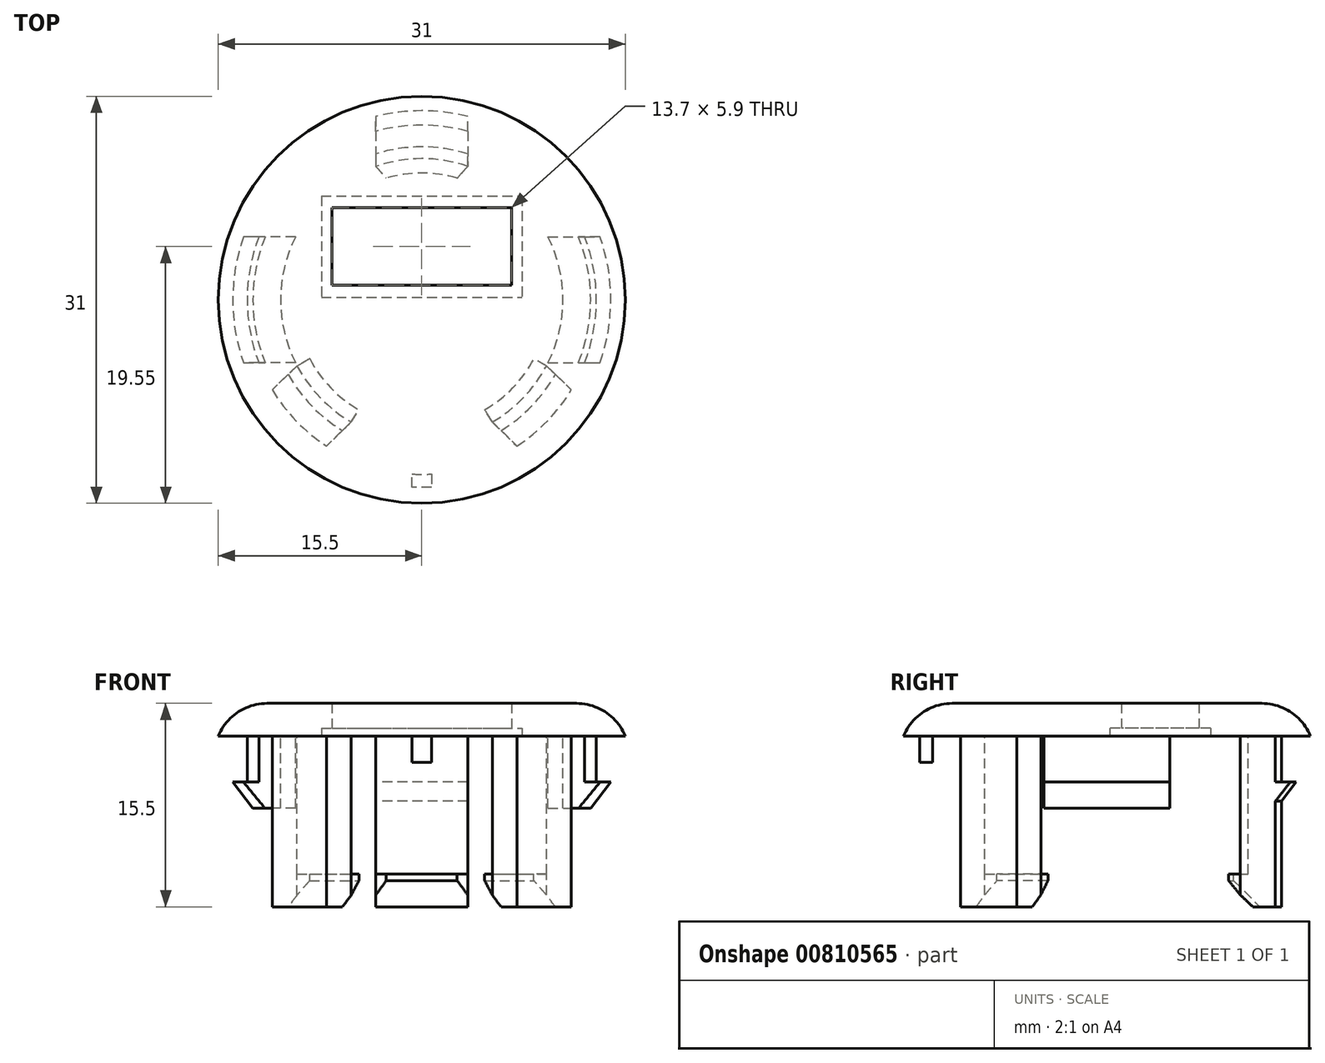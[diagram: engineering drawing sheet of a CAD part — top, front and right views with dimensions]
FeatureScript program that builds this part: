
annotation { "Feature Type Name" : "Feature", "Feature Type Description" : "" }
export const myFeature = defineFeature(function(context is Context, id is Id, definition is map)
    precondition{}
    {
        {
            var Q0;
            Q0=qCreatedBy(makeId("Top.planeOp"),FACE);
            var sketch = newSketch(context, id + "F0", { "sketchPlane" : qUnion([Q0])});
            skCircle(sketch, "E0", {"center": v(0, 0) * mm, "radius": 10.75 * mm});
            skLineSegment(sketch, "E1.bottom", {"start": v(-6.85, 7) * mm, "end": v(6.85, 7) * mm});
            skLineSegment(sketch, "E1.top", {"start": v(-6.85, 1.1) * mm, "end": v(6.85, 1.1) * mm});
            skLineSegment(sketch, "E1.left", {"start": v(-6.85, 7) * mm, "end": v(-6.85, 1.1) * mm});
            skLineSegment(sketch, "E1.right", {"start": v(6.85, 7) * mm, "end": v(6.85, 1.1) * mm});
            skPoint(sketch, "E1.middle", {"position": v(0, 4.05) * mm});
            skCircle(sketch, "E2", {"center": v(0, 0) * mm, "radius": 13.3 * mm});
            skLineSegment(sketch, "E3", {"start": v(-3.5, 12.83) * mm, "end": v(-3.5, 10.16) * mm});
            skLineSegment(sketch, "E4", {"start": v(3.5, 12.83) * mm, "end": v(3.5, 10.16) * mm});
            skLineSegment(sketch, "E5", {"start": v(9.5, -5.04) * mm, "end": v(11.4, -6.86) * mm});
            skLineSegment(sketch, "E6", {"start": v(5.37, -9.31) * mm, "end": v(7.25, -11.15) * mm});
            skLineSegment(sketch, "E7", {"start": v(-5.37, -9.31) * mm, "end": v(-7.25, -11.15) * mm});
            skLineSegment(sketch, "E8", {"start": v(-9.5, -5.04) * mm, "end": v(-11.4, -6.86) * mm});
            skPoint(sketch, "E9", {"position": v(-7.73, -7.47) * mm});
            skPoint(sketch, "E10", {"position": v(7.73, -7.47) * mm});
            skLineSegment(sketch, "E11", {"start": v(0, 0) * mm, "end": v(7.73, -7.47) * mm});
            skLineSegment(sketch, "E12", {"start": v(0, 0) * mm, "end": v(-7.73, -7.47) * mm});
            skLineSegment(sketch, "E13", {"start": v(-7.73, -7.47) * mm, "end": v(-9.57, -9.24) * mm});
            skLineSegment(sketch, "E14", {"start": v(7.73, -7.47) * mm, "end": v(9.57, -9.24) * mm});
            skCircle(sketch, "E15", {"center": v(0, 0) * mm, "radius": 9.65 * mm});
            skLineSegment(sketch, "E16", {"start": v(9.5, -5.04) * mm, "end": v(8.54, -4.5) * mm});
            skLineSegment(sketch, "E17", {"start": v(5.37, -9.31) * mm, "end": v(4.79, -8.38) * mm});
            skLineSegment(sketch, "E18", {"start": v(-5.37, -9.31) * mm, "end": v(-4.79, -8.38) * mm});
            skLineSegment(sketch, "E19", {"start": v(-9.5, -5.04) * mm, "end": v(-8.54, -4.5) * mm});
            skLineSegment(sketch, "E20", {"start": v(3.5, 10.16) * mm, "end": v(2.7, 9.26) * mm});
            skLineSegment(sketch, "E21", {"start": v(-3.5, 10.16) * mm, "end": v(-2.7, 9.26) * mm});
            skCircle(sketch, "E22", {"center": v(0, 0) * mm, "radius": 14.4 * mm});
            skLineSegment(sketch, "E23", {"start": v(9.62, -4.8) * mm, "end": v(12.4, -4.8) * mm});
            skLineSegment(sketch, "E24", {"start": v(12.4, -4.8) * mm, "end": v(13.58, -4.8) * mm});
            skLineSegment(sketch, "E25", {"start": v(9.62, 4.8) * mm, "end": v(12.4, 4.8) * mm});
            skLineSegment(sketch, "E26", {"start": v(12.4, 4.8) * mm, "end": v(13.58, 4.8) * mm});
            skLineSegment(sketch, "E27", {"start": v(-9.62, 4.8) * mm, "end": v(-12.4, 4.8) * mm});
            skLineSegment(sketch, "E28", {"start": v(-12.4, 4.8) * mm, "end": v(-13.58, 4.8) * mm});
            skLineSegment(sketch, "E29", {"start": v(-9.62, -4.8) * mm, "end": v(-12.4, -4.8) * mm});
            skLineSegment(sketch, "E30", {"start": v(-12.4, -4.8) * mm, "end": v(-13.58, -4.8) * mm});
            skLineSegment(sketch, "E31", {"start": v(0.75, -13.28) * mm, "end": v(0.75, -14.28) * mm});
            skLineSegment(sketch, "E32", {"start": v(0.75, -14.28) * mm, "end": v(-0.75, -14.28) * mm});
            skLineSegment(sketch, "E33", {"start": v(-0.75, -14.28) * mm, "end": v(-0.75, -13.28) * mm});
            skLineSegment(sketch, "E34.bottom", {"start": v(-7.65, 7.9) * mm, "end": v(7.65, 7.9) * mm});
            skLineSegment(sketch, "E34.top", {"start": v(-7.65, 0.2) * mm, "end": v(7.65, 0.2) * mm});
            skLineSegment(sketch, "E34.left", {"start": v(-7.65, 7.9) * mm, "end": v(-7.65, 0.2) * mm});
            skLineSegment(sketch, "E34.right", {"start": v(7.65, 7.9) * mm, "end": v(7.65, 0.2) * mm});
            skCircle(sketch, "E35", {"center": v(0, 0) * mm, "radius": 15.5 * mm});
            skLineSegment(sketch, "E36", {"start": v(-3.5, 12.83) * mm, "end": v(-3.5, 13.97) * mm});
            skLineSegment(sketch, "E37", {"start": v(3.5, 12.83) * mm, "end": v(3.5, 13.97) * mm});
            skSolve(sketch);
        }
        {
            var Q0;
            Q0=makeQuery(id+"F0.imprint","IMPRINT",FACE,{"disambiguationData":[TD([[makeQuery(id+"F0.imprint","IMPRINT",EDGE,{"derivedFrom":sQuery(id+"F0.wireOp",EDGE,"E0")}),1.0]])]});
            var Q1;
            Q1=makeQuery(id+"F0.imprint","IMPRINT",FACE,{"disambiguationData":[TD([[makeQuery(id+"F0.imprint","IMPRINT",EDGE,{"derivedFrom":sQuery(id+"F0.wireOp",EDGE,"E0")}),-1.0]])]});
            var Q2;
            {var subQ0=sQuery(id+"F0.wireOp",EDGE,"E11");Q2=makeQuery(id+"F0.imprint","IMPRINT",FACE,{"disambiguationData":[TD([[makeQuery(id+"F0.imprint","IMPRINT",EDGE,{"derivedFrom":subQ0}),-1.0]])]});}
            var Q3;
            Q3=makeQuery(id+"F0.imprint","IMPRINT",FACE,{"disambiguationData":[TD([[makeQuery(id+"F0.imprint","IMPRINT",EDGE,{"derivedFrom":sQuery(id+"F0.wireOp",EDGE,"E1.bottom")}),1.0]])]});
            var Q4;
            {var subQ2=sQuery(id+"F0.wireOp",EDGE,"E12");var subQ4=sQuery(id+"F0.wireOp",EDGE,"E11");var subQ5=makeQuery(id+"F0.imprint","INTERSECT",VERTEX,{"derivedFrom":[subQ4,subQ2]});Q4=makeQuery(id+"F0.imprint","IMPRINT",FACE,{"disambiguationData":[TD([[makeQuery(id+"F0.imprint","IMPRINT",EDGE,{"disambiguationData":[TD([[subQ5,-1.0]])],"derivedFrom":subQ4}),-1.0]])]});}
            var Q5;
            {var subQ9=sQuery(id+"F0.wireOp",EDGE,"E1.top");Q5=makeQuery(id+"F0.imprint","IMPRINT",FACE,{"disambiguationData":[TD([[makeQuery(id+"F0.imprint","IMPRINT",EDGE,{"derivedFrom":subQ9}),-1.0]])]});}
            var Q6;
            {var subQ5=sQuery(id+"F0.wireOp",EDGE,"E16");Q6=makeQuery(id+"F0.imprint","IMPRINT",FACE,{"disambiguationData":[TD([[makeQuery(id+"F0.imprint","IMPRINT",EDGE,{"derivedFrom":subQ5}),-1.0]])]});}
            var Q7;
            {var subQ8=sQuery(id+"F0.wireOp",EDGE,"E19");Q7=makeQuery(id+"F0.imprint","IMPRINT",FACE,{"disambiguationData":[TD([[makeQuery(id+"F0.imprint","IMPRINT",EDGE,{"derivedFrom":subQ8}),1.0]])]});}
            var Q8;
            Q8=makeQuery(id+"F0.imprint","IMPRINT",FACE,{"disambiguationData":[TD([[makeQuery(id+"F0.imprint","IMPRINT",EDGE,{"derivedFrom":sQuery(id+"F0.wireOp",EDGE,"E22")}),1.0]])]});
            var Q9;
            {var subQ0=sQuery(id+"F0.wireOp",EDGE,"E6");Q9=makeQuery(id+"F0.imprint","IMPRINT",FACE,{"disambiguationData":[TD([[makeQuery(id+"F0.imprint","IMPRINT",EDGE,{"derivedFrom":subQ0}),-1.0]])]});}
            var Q10;
            {var subQ4=sQuery(id+"F0.wireOp",EDGE,"V6FVYBft-MwFG-yFSS-5wyN-DWkYvqWRzlp1");Q10=makeQuery(id+"F0.imprint","IMPRINT",FACE,{"disambiguationData":[TD([[makeQuery(id+"F0.imprint","IMPRINT",EDGE,{"derivedFrom":subQ4}),1.0]])]});}
            var Q11;
            {var subQ0=sQuery(id+"F0.wireOp",EDGE,"V6FVYBft-MwFG-yFSS-5wyN-DWkYvqWRzlp1");Q11=makeQuery(id+"F0.imprint","IMPRINT",FACE,{"disambiguationData":[TD([[makeQuery(id+"F0.imprint","IMPRINT",EDGE,{"derivedFrom":subQ0}),-1.0]])]});}
            var Q12;
            {var subQ2=sQuery(id+"F0.wireOp",EDGE,"E20");Q12=makeQuery(id+"F0.imprint","IMPRINT",FACE,{"disambiguationData":[TD([[makeQuery(id+"F0.imprint","IMPRINT",EDGE,{"derivedFrom":subQ2}),-1.0]])]});}
            var Q13;
            {var subQ0=sQuery(id+"F0.wireOp",EDGE,"E26");Q13=makeQuery(id+"F0.imprint","IMPRINT",FACE,{"disambiguationData":[TD([[makeQuery(id+"F0.imprint","IMPRINT",EDGE,{"derivedFrom":subQ0}),1.0]])]});}
            var Q14;
            {var subQ0=sQuery(id+"F0.wireOp",EDGE,"E16");Q14=makeQuery(id+"F0.imprint","IMPRINT",FACE,{"disambiguationData":[TD([[makeQuery(id+"F0.imprint","IMPRINT",EDGE,{"derivedFrom":subQ0}),1.0]])]});}
            var Q15;
            {var subQ0=sQuery(id+"F0.wireOp",EDGE,"E17");Q15=makeQuery(id+"F0.imprint","IMPRINT",FACE,{"disambiguationData":[TD([[makeQuery(id+"F0.imprint","IMPRINT",EDGE,{"derivedFrom":subQ0}),1.0]])]});}
            var Q16;
            {var subQ0=sQuery(id+"F0.wireOp",EDGE,"E18");Q16=makeQuery(id+"F0.imprint","IMPRINT",FACE,{"disambiguationData":[TD([[makeQuery(id+"F0.imprint","IMPRINT",EDGE,{"derivedFrom":subQ0}),1.0]])]});}
            var Q17;
            {var subQ2=sQuery(id+"F0.wireOp",EDGE,"IsypwA4p-UdKw-Pqgo-aUDO-kLr4VSGxCjIw");Q17=makeQuery(id+"F0.imprint","IMPRINT",FACE,{"disambiguationData":[TD([[makeQuery(id+"F0.imprint","IMPRINT",EDGE,{"derivedFrom":subQ2}),1.0]])]});}
            var Q18;
            {var subQ0=sQuery(id+"F0.wireOp",EDGE,"E19");Q18=makeQuery(id+"F0.imprint","IMPRINT",FACE,{"disambiguationData":[TD([[makeQuery(id+"F0.imprint","IMPRINT",EDGE,{"derivedFrom":subQ0}),-1.0]])]});}
            var Q19;
            {var subQ0=sQuery(id+"F0.wireOp",EDGE,"E24");Q19=makeQuery(id+"F0.imprint","IMPRINT",FACE,{"disambiguationData":[TD([[makeQuery(id+"F0.imprint","IMPRINT",EDGE,{"derivedFrom":subQ0}),-1.0]])]});}
            var Q20;
            {var subQ0=sQuery(id+"F0.wireOp",EDGE,"E31");Q20=makeQuery(id+"F0.imprint","IMPRINT",FACE,{"disambiguationData":[TD([[makeQuery(id+"F0.imprint","IMPRINT",EDGE,{"derivedFrom":subQ0}),-1.0]])]});}
            var Q21;
            {var subQ0=sQuery(id+"F0.wireOp",EDGE,"E8");Q21=makeQuery(id+"F0.imprint","IMPRINT",FACE,{"disambiguationData":[TD([[makeQuery(id+"F0.imprint","IMPRINT",EDGE,{"derivedFrom":subQ0}),-1.0]])]});}
            var Q22;
            {var subQ3=sQuery(id+"F0.wireOp",EDGE,"E34.bottom");var subQ7=sQuery(id+"F0.wireOp",EDGE,"E0");var subQ8=makeQuery(id+"F0.imprint","INTERSECT",VERTEX,{"disambiguationData":[OD(1.0)],"derivedFrom":[subQ7,subQ3]});Q22=makeQuery(id+"F0.imprint","IMPRINT",FACE,{"disambiguationData":[TD([[makeQuery(id+"F0.imprint","IMPRINT",EDGE,{"disambiguationData":[TD([[subQ8,-1.0]])],"derivedFrom":subQ7}),1.0]])]});}
            var Q23;
            {var subQ0=sQuery(id+"F0.wireOp",EDGE,"E34.bottom");var subQ1=sQuery(id+"F0.wireOp",EDGE,"E0");var subQ2=makeQuery(id+"F0.imprint","INTERSECT",VERTEX,{"disambiguationData":[OD(1.0)],"derivedFrom":[subQ1,subQ0]});Q23=makeQuery(id+"F0.imprint","IMPRINT",FACE,{"disambiguationData":[TD([[makeQuery(id+"F0.imprint","IMPRINT",EDGE,{"disambiguationData":[TD([[subQ2,-1.0]])],"derivedFrom":subQ1}),-1.0]])]});}
            var Q24;
            {var subQ0=sQuery(id+"F0.wireOp",EDGE,"E34.right");var subQ1=sQuery(id+"F0.wireOp",EDGE,"E0");var subQ2=makeQuery(id+"F0.imprint","INTERSECT",VERTEX,{"derivedFrom":[subQ1,subQ0]});Q24=makeQuery(id+"F0.imprint","IMPRINT",FACE,{"disambiguationData":[TD([[makeQuery(id+"F0.imprint","IMPRINT",EDGE,{"disambiguationData":[TD([[subQ2,-1.0]])],"derivedFrom":subQ1}),-1.0]])]});}
            var Q25;
            {var subQ3=sQuery(id+"F0.wireOp",EDGE,"E34.right");var subQ8=sQuery(id+"F0.wireOp",EDGE,"E0");var subQ9=makeQuery(id+"F0.imprint","INTERSECT",VERTEX,{"derivedFrom":[subQ8,subQ3]});Q25=makeQuery(id+"F0.imprint","IMPRINT",FACE,{"disambiguationData":[TD([[makeQuery(id+"F0.imprint","IMPRINT",EDGE,{"disambiguationData":[TD([[subQ9,-1.0]])],"derivedFrom":subQ8}),1.0]])]});}
            var Q26;
            {var subQ0=sQuery(id+"F0.wireOp",EDGE,"E3");Q26=makeQuery(id+"F0.imprint","IMPRINT",FACE,{"disambiguationData":[TD([[makeQuery(id+"F0.imprint","IMPRINT",EDGE,{"derivedFrom":subQ0}),1.0]])]});}
            var Q27;
            {var subQ0=sQuery(id+"F0.wireOp",EDGE,"E21");Q27=makeQuery(id+"F0.imprint","IMPRINT",FACE,{"disambiguationData":[TD([[makeQuery(id+"F0.imprint","IMPRINT",EDGE,{"derivedFrom":subQ0}),-1.0]])]});}
            var Q28;
            {var subQ0=sQuery(id+"F0.wireOp",EDGE,"E15");var subQ1=makeQuery(id+"F0.imprint","INTERSECT",VERTEX,{"derivedFrom":[subQ0,sQuery(id+"F0.wireOp",EDGE,"E20")]});Q28=makeQuery(id+"F0.imprint","IMPRINT",FACE,{"disambiguationData":[TD([[makeQuery(id+"F0.imprint","IMPRINT",EDGE,{"disambiguationData":[TD([[subQ1,1.0]])],"derivedFrom":subQ0}),1.0]])]});}
            var Q29;
            {var subQ0=sQuery(id+"F0.wireOp",EDGE,"E20");Q29=makeQuery(id+"F0.imprint","IMPRINT",FACE,{"disambiguationData":[TD([[makeQuery(id+"F0.imprint","IMPRINT",EDGE,{"derivedFrom":subQ0}),1.0]])]});}
            var Q30;
            {var subQ0=sQuery(id+"F0.wireOp",EDGE,"E5");Q30=makeQuery(id+"F0.imprint","IMPRINT",FACE,{"disambiguationData":[TD([[makeQuery(id+"F0.imprint","IMPRINT",EDGE,{"derivedFrom":subQ0}),1.0]])]});}
            var Q31;
            {var subQ0=sQuery(id+"F0.wireOp",EDGE,"E5");Q31=makeQuery(id+"F0.imprint","IMPRINT",FACE,{"disambiguationData":[TD([[makeQuery(id+"F0.imprint","IMPRINT",EDGE,{"derivedFrom":subQ0}),-1.0]])]});}
            var Q32;
            {var subQ0=sQuery(id+"F0.wireOp",EDGE,"E6");Q32=makeQuery(id+"F0.imprint","IMPRINT",FACE,{"disambiguationData":[TD([[makeQuery(id+"F0.imprint","IMPRINT",EDGE,{"derivedFrom":subQ0}),1.0]])]});}
            var Q33;
            {var subQ0=sQuery(id+"F0.wireOp",EDGE,"E23");Q33=makeQuery(id+"F0.imprint","IMPRINT",FACE,{"disambiguationData":[TD([[makeQuery(id+"F0.imprint","IMPRINT",EDGE,{"derivedFrom":subQ0}),1.0]])]});}
            var Q34;
            {var subQ8=sQuery(id+"F0.wireOp",EDGE,"E34.top");Q34=makeQuery(id+"F0.imprint","IMPRINT",FACE,{"disambiguationData":[TD([[makeQuery(id+"F0.imprint","IMPRINT",EDGE,{"derivedFrom":subQ8}),-1.0]])]});}
            var Q35;
            {var subQ0=sQuery(id+"F0.wireOp",EDGE,"E7");Q35=makeQuery(id+"F0.imprint","IMPRINT",FACE,{"disambiguationData":[TD([[makeQuery(id+"F0.imprint","IMPRINT",EDGE,{"derivedFrom":subQ0}),-1.0]])]});}
            var Q36;
            {var subQ0=sQuery(id+"F0.wireOp",EDGE,"E8");Q36=makeQuery(id+"F0.imprint","IMPRINT",FACE,{"disambiguationData":[TD([[makeQuery(id+"F0.imprint","IMPRINT",EDGE,{"derivedFrom":subQ0}),1.0]])]});}
            var Q37;
            {var subQ0=sQuery(id+"F0.wireOp",EDGE,"E27");Q37=makeQuery(id+"F0.imprint","IMPRINT",FACE,{"disambiguationData":[TD([[makeQuery(id+"F0.imprint","IMPRINT",EDGE,{"derivedFrom":subQ0}),1.0]])]});}
            var Q38;
            {var subQ1=sQuery(id+"F0.wireOp",EDGE,"E1.right");var subQ5=sQuery(id+"F0.wireOp",EDGE,"E1.bottom");var subQ9=makeQuery(id+"F0.imprint","INTERSECT",VERTEX,{"derivedFrom":[subQ5,subQ1]});Q38=makeQuery(id+"F0.imprint","IMPRINT",FACE,{"disambiguationData":[TD([[makeQuery(id+"F0.imprint","IMPRINT",EDGE,{"disambiguationData":[TD([[subQ9,1.0]])],"derivedFrom":subQ5}),1.0]])]});}
            var Q39;
            {var subQ1=sQuery(id+"F0.wireOp",EDGE,"E1.left");var subQ7=sQuery(id+"F0.wireOp",EDGE,"E1.bottom");var subQ8=makeQuery(id+"F0.imprint","INTERSECT",VERTEX,{"derivedFrom":[subQ7,subQ1]});Q39=makeQuery(id+"F0.imprint","IMPRINT",FACE,{"disambiguationData":[TD([[makeQuery(id+"F0.imprint","IMPRINT",EDGE,{"disambiguationData":[TD([[subQ8,-1.0]])],"derivedFrom":subQ7}),1.0]])]});}
            var Q40;
            Q40=makeQuery(id+"F0.imprint","IMPRINT",FACE,{"disambiguationData":[TD([[makeQuery(id+"F0.imprint","IMPRINT",EDGE,{"derivedFrom":sQuery(id+"F0.wireOp",EDGE,"E35")}),1.0]])]});
            extrude(context, id + "F1", {"entities" : qUnion([Q0, Q1, Q2, Q3, Q4, Q5, Q6, Q7, Q8, Q9, Q10, Q11, Q12, Q13, Q14, Q15, Q16, Q17, Q18, Q19, Q20, Q21, Q22, Q23, Q24, Q25, Q26, Q27, Q28, Q29, Q30, Q31, Q32, Q33, Q34, Q35, Q36, Q37, Q38, Q39, Q40]), "depth" : 2.5 * mm, "offsetDistance" : 25 * mm});
        }
        {
            var Q0;
            Q0=makeQuery(id+"F1.opExtrude","CAP_EDGE",EDGE,{"disambiguationData":[OSD([sQuery(id+"F0.wireOp",EDGE,"E35")])],"isStart":false});
            fillet(context, id + "F2", {"entities" : qUnion([Q0]), "radius" : 4 * mm, "tangentPropagation" : true, "allowEdgeOverflow" : false});
        }
        {
            var Q0;
            {var subQ6=sQuery(id+"F0.wireOp",EDGE,"E1.top");Q0=makeQuery(id+"F0.imprint","IMPRINT",FACE,{"disambiguationData":[TD([[makeQuery(id+"F0.imprint","IMPRINT",EDGE,{"derivedFrom":subQ6}),-1.0]])]});}
            var Q1;
            {var subQ1=sQuery(id+"F0.wireOp",EDGE,"E1.left");var subQ7=sQuery(id+"F0.wireOp",EDGE,"E1.bottom");var subQ8=makeQuery(id+"F0.imprint","INTERSECT",VERTEX,{"derivedFrom":[subQ7,subQ1]});Q1=makeQuery(id+"F0.imprint","IMPRINT",FACE,{"disambiguationData":[TD([[makeQuery(id+"F0.imprint","IMPRINT",EDGE,{"disambiguationData":[TD([[subQ8,-1.0]])],"derivedFrom":subQ7}),1.0]])]});}
            var Q2;
            {var subQ0=sQuery(id+"F0.wireOp",EDGE,"E15");var subQ1=sQuery(id+"F0.wireOp",EDGE,"E1.bottom");var subQ2=makeQuery(id+"F0.imprint","INTERSECT",VERTEX,{"disambiguationData":[OD(0.0)],"derivedFrom":[subQ1,subQ0]});Q2=makeQuery(id+"F0.imprint","IMPRINT",FACE,{"disambiguationData":[TD([[makeQuery(id+"F0.imprint","IMPRINT",EDGE,{"disambiguationData":[TD([[subQ2,-1.0]])],"derivedFrom":subQ1}),1.0]])]});}
            var Q3;
            {var subQ1=sQuery(id+"F0.wireOp",EDGE,"E1.right");var subQ5=sQuery(id+"F0.wireOp",EDGE,"E1.bottom");var subQ9=makeQuery(id+"F0.imprint","INTERSECT",VERTEX,{"derivedFrom":[subQ5,subQ1]});Q3=makeQuery(id+"F0.imprint","IMPRINT",FACE,{"disambiguationData":[TD([[makeQuery(id+"F0.imprint","IMPRINT",EDGE,{"disambiguationData":[TD([[subQ9,1.0]])],"derivedFrom":subQ5}),1.0]])]});}
            var Q4;
            {var subQ0=sQuery(id+"F0.wireOp",EDGE,"E34.right");var subQ1=sQuery(id+"F0.wireOp",EDGE,"E0");var subQ2=makeQuery(id+"F0.imprint","INTERSECT",VERTEX,{"derivedFrom":[subQ1,subQ0]});Q4=makeQuery(id+"F0.imprint","IMPRINT",FACE,{"disambiguationData":[TD([[makeQuery(id+"F0.imprint","IMPRINT",EDGE,{"disambiguationData":[TD([[subQ2,-1.0]])],"derivedFrom":subQ1}),-1.0]])]});}
            var Q5;
            {var subQ0=sQuery(id+"F0.wireOp",EDGE,"E34.bottom");var subQ1=sQuery(id+"F0.wireOp",EDGE,"E0");var subQ2=makeQuery(id+"F0.imprint","INTERSECT",VERTEX,{"disambiguationData":[OD(1.0)],"derivedFrom":[subQ1,subQ0]});Q5=makeQuery(id+"F0.imprint","IMPRINT",FACE,{"disambiguationData":[TD([[makeQuery(id+"F0.imprint","IMPRINT",EDGE,{"disambiguationData":[TD([[subQ2,-1.0]])],"derivedFrom":subQ1}),-1.0]])]});}
            extrude(context, id + "F3", {"entities" : qUnion([Q0, Q1, Q2, Q3, Q4, Q5]), "operationType" : NewBodyOperationType.REMOVE, "depth" : .6 * mm, "offsetDistance" : 25 * mm});
        }
        {
            var Q0;
            {var subQ0=sQuery(id+"F0.wireOp",EDGE,"V6FVYBft-MwFG-yFSS-5wyN-DWkYvqWRzlp1");Q0=makeQuery(id+"F0.imprint","IMPRINT",FACE,{"disambiguationData":[TD([[makeQuery(id+"F0.imprint","IMPRINT",EDGE,{"derivedFrom":subQ0}),-1.0]])]});}
            var Q1;
            {var subQ0=sQuery(id+"F0.wireOp",EDGE,"E31");Q1=makeQuery(id+"F0.imprint","IMPRINT",FACE,{"disambiguationData":[TD([[makeQuery(id+"F0.imprint","IMPRINT",EDGE,{"derivedFrom":subQ0}),-1.0]])]});}
            extrude(context, id + "F4", {"entities" : qUnion([Q0, Q1]), "operationType" : NewBodyOperationType.ADD, "oppositeDirection" : true, "depth" : 2 * mm, "offsetDistance" : 25 * mm});
        }
        {
            var Q0;
            {var subQ0=sQuery(id+"F0.wireOp",EDGE,"E7");Q0=makeQuery(id+"F0.imprint","IMPRINT",FACE,{"disambiguationData":[TD([[makeQuery(id+"F0.imprint","IMPRINT",EDGE,{"derivedFrom":subQ0}),-1.0]])]});}
            var Q1;
            {var subQ0=sQuery(id+"F0.wireOp",EDGE,"E6");Q1=makeQuery(id+"F0.imprint","IMPRINT",FACE,{"disambiguationData":[TD([[makeQuery(id+"F0.imprint","IMPRINT",EDGE,{"derivedFrom":subQ0}),1.0]])]});}
            var Q2;
            {var subQ0=sQuery(id+"F0.wireOp",EDGE,"E5");Q2=makeQuery(id+"F0.imprint","IMPRINT",FACE,{"disambiguationData":[TD([[makeQuery(id+"F0.imprint","IMPRINT",EDGE,{"derivedFrom":subQ0}),-1.0]])]});}
            var Q3;
            {var subQ0=sQuery(id+"F0.wireOp",EDGE,"E3");Q3=makeQuery(id+"F0.imprint","IMPRINT",FACE,{"disambiguationData":[TD([[makeQuery(id+"F0.imprint","IMPRINT",EDGE,{"derivedFrom":subQ0}),1.0]])]});}
            var Q4;
            {var subQ0=sQuery(id+"F0.wireOp",EDGE,"E8");Q4=makeQuery(id+"F0.imprint","IMPRINT",FACE,{"disambiguationData":[TD([[makeQuery(id+"F0.imprint","IMPRINT",EDGE,{"derivedFrom":subQ0}),1.0]])]});}
            var Q5;
            {var subQ2=sQuery(id+"F0.wireOp",EDGE,"E20");Q5=makeQuery(id+"F0.imprint","IMPRINT",FACE,{"disambiguationData":[TD([[makeQuery(id+"F0.imprint","IMPRINT",EDGE,{"derivedFrom":subQ2}),-1.0]])]});}
            var Q6;
            {var subQ0=sQuery(id+"F0.wireOp",EDGE,"E19");Q6=makeQuery(id+"F0.imprint","IMPRINT",FACE,{"disambiguationData":[TD([[makeQuery(id+"F0.imprint","IMPRINT",EDGE,{"derivedFrom":subQ0}),-1.0]])]});}
            var Q7;
            {var subQ0=sQuery(id+"F0.wireOp",EDGE,"E18");Q7=makeQuery(id+"F0.imprint","IMPRINT",FACE,{"disambiguationData":[TD([[makeQuery(id+"F0.imprint","IMPRINT",EDGE,{"derivedFrom":subQ0}),1.0]])]});}
            var Q8;
            {var subQ0=sQuery(id+"F0.wireOp",EDGE,"E16");Q8=makeQuery(id+"F0.imprint","IMPRINT",FACE,{"disambiguationData":[TD([[makeQuery(id+"F0.imprint","IMPRINT",EDGE,{"derivedFrom":subQ0}),1.0]])]});}
            var Q9;
            {var subQ0=sQuery(id+"F0.wireOp",EDGE,"E17");Q9=makeQuery(id+"F0.imprint","IMPRINT",FACE,{"disambiguationData":[TD([[makeQuery(id+"F0.imprint","IMPRINT",EDGE,{"derivedFrom":subQ0}),-1.0]])]});}
            extrude(context, id + "F5", {"entities" : qUnion([Q0, Q1, Q2, Q3, Q4, Q5, Q6, Q7, Q8, Q9]), "operationType" : NewBodyOperationType.ADD, "oppositeDirection" : true, "depth" : 13 * mm, "offsetDistance" : 25 * mm});
        }
        {
            var Q0;
            {var subQ0=sQuery(id+"F0.wireOp",EDGE,"E17");Q0=makeQuery(id+"F0.imprint","IMPRINT",FACE,{"disambiguationData":[TD([[makeQuery(id+"F0.imprint","IMPRINT",EDGE,{"derivedFrom":subQ0}),-1.0]])]});}
            var Q1;
            {var subQ0=sQuery(id+"F0.wireOp",EDGE,"E16");Q1=makeQuery(id+"F0.imprint","IMPRINT",FACE,{"disambiguationData":[TD([[makeQuery(id+"F0.imprint","IMPRINT",EDGE,{"derivedFrom":subQ0}),1.0]])]});}
            var Q2;
            {var subQ2=sQuery(id+"F0.wireOp",EDGE,"E20");Q2=makeQuery(id+"F0.imprint","IMPRINT",FACE,{"disambiguationData":[TD([[makeQuery(id+"F0.imprint","IMPRINT",EDGE,{"derivedFrom":subQ2}),-1.0]])]});}
            var Q3;
            {var subQ0=sQuery(id+"F0.wireOp",EDGE,"E18");Q3=makeQuery(id+"F0.imprint","IMPRINT",FACE,{"disambiguationData":[TD([[makeQuery(id+"F0.imprint","IMPRINT",EDGE,{"derivedFrom":subQ0}),1.0]])]});}
            var Q4;
            {var subQ0=sQuery(id+"F0.wireOp",EDGE,"E19");Q4=makeQuery(id+"F0.imprint","IMPRINT",FACE,{"disambiguationData":[TD([[makeQuery(id+"F0.imprint","IMPRINT",EDGE,{"derivedFrom":subQ0}),-1.0]])]});}
            var Q5;
            {var subQ0=sQuery(id+"F0.wireOp",EDGE,"E34.right");var subQ1=sQuery(id+"F0.wireOp",EDGE,"E0");var subQ2=makeQuery(id+"F0.imprint","INTERSECT",VERTEX,{"derivedFrom":[subQ1,subQ0]});Q5=makeQuery(id+"F0.imprint","IMPRINT",FACE,{"disambiguationData":[TD([[makeQuery(id+"F0.imprint","IMPRINT",EDGE,{"disambiguationData":[TD([[subQ2,-1.0]])],"derivedFrom":subQ1}),-1.0]])]});}
            extrude(context, id + "F6", {"entities" : qUnion([Q0, Q1, Q2, Q3, Q4, Q5]), "operationType" : NewBodyOperationType.REMOVE, "oppositeDirection" : true, "depth" : 10.5 * mm, "offsetDistance" : 25 * mm});
        }
        {
            var Q0;
            {var subQ0=sQuery(id+"F0.wireOp",EDGE,"E15");Q0=makeQuery(id+"F5.opExtrude","CAP_EDGE",EDGE,{"disambiguationData":[OSD([subQ0]),TDD([makeQuery(id+"F0.imprint","IMPRINT",EDGE,{"disambiguationData":[TD([[makeQuery(id+"F0.imprint","INTERSECT",VERTEX,{"derivedFrom":[subQ0,sQuery(id+"F0.wireOp",EDGE,"E19")]}),-1.0]])],"derivedFrom":subQ0}),makeQuery(id+"F0.imprint","IMPRINT",EDGE,{"disambiguationData":[TD([[makeQuery(id+"F0.imprint","INTERSECT",VERTEX,{"derivedFrom":[subQ0,sQuery(id+"F0.wireOp",EDGE,"E18")]}),1.0]])],"derivedFrom":subQ0})])],"isStart":false});}
            var Q1;
            {var subQ0=sQuery(id+"F0.wireOp",EDGE,"E15");Q1=makeQuery(id+"F5.opExtrude","CAP_EDGE",EDGE,{"disambiguationData":[OSD([subQ0]),TDD([makeQuery(id+"F0.imprint","IMPRINT",EDGE,{"disambiguationData":[TD([[makeQuery(id+"F0.imprint","INTERSECT",VERTEX,{"derivedFrom":[subQ0,sQuery(id+"F0.wireOp",EDGE,"E17")]}),-1.0]])],"derivedFrom":subQ0}),makeQuery(id+"F0.imprint","IMPRINT",EDGE,{"disambiguationData":[TD([[makeQuery(id+"F0.imprint","INTERSECT",VERTEX,{"derivedFrom":[subQ0,sQuery(id+"F0.wireOp",EDGE,"E16")]}),1.0]])],"derivedFrom":subQ0})])],"isStart":false});}
            var Q2;
            {var subQ0=sQuery(id+"F0.wireOp",EDGE,"E15");Q2=makeQuery(id+"F5.opExtrude","CAP_EDGE",EDGE,{"disambiguationData":[OSD([subQ0]),TDD([makeQuery(id+"F0.imprint","IMPRINT",EDGE,{"disambiguationData":[TD([[makeQuery(id+"F0.imprint","INTERSECT",VERTEX,{"derivedFrom":[subQ0,sQuery(id+"F0.wireOp",EDGE,"E20")]}),-1.0]])],"derivedFrom":subQ0})])],"isStart":false});}
            chamfer(context, id + "F7", {"entities" : qUnion([Q0, Q1, Q2]), "chamferType" : ChamferType.OFFSET_ANGLE, "width" : 2 * mm, "oppositeDirection" : true, "angle" : 45 * degree, "tangentPropagation" : true});
        }
        {
            var Q0;
            {var subQ0=sQuery(id+"F0.wireOp",EDGE,"E23");Q0=makeQuery(id+"F0.imprint","IMPRINT",FACE,{"disambiguationData":[TD([[makeQuery(id+"F0.imprint","IMPRINT",EDGE,{"derivedFrom":subQ0}),1.0]])]});}
            var Q1;
            {var subQ0=sQuery(id+"F0.wireOp",EDGE,"E24");Q1=makeQuery(id+"F0.imprint","IMPRINT",FACE,{"disambiguationData":[TD([[makeQuery(id+"F0.imprint","IMPRINT",EDGE,{"derivedFrom":subQ0}),1.0]])]});}
            var Q2;
            {var subQ0=sQuery(id+"F0.wireOp",EDGE,"E28");Q2=makeQuery(id+"F0.imprint","IMPRINT",FACE,{"disambiguationData":[TD([[makeQuery(id+"F0.imprint","IMPRINT",EDGE,{"derivedFrom":subQ0}),1.0]])]});}
            var Q3;
            {var subQ0=sQuery(id+"F0.wireOp",EDGE,"E27");Q3=makeQuery(id+"F0.imprint","IMPRINT",FACE,{"disambiguationData":[TD([[makeQuery(id+"F0.imprint","IMPRINT",EDGE,{"derivedFrom":subQ0}),1.0]])]});}
            var Q4;
            {var subQ0=sQuery(id+"F0.wireOp",EDGE,"E36");Q4=makeQuery(id+"F0.imprint","IMPRINT",FACE,{"disambiguationData":[TD([[makeQuery(id+"F0.imprint","IMPRINT",EDGE,{"derivedFrom":subQ0}),-1.0]])]});}
            extrude(context, id + "F8", {"entities" : qUnion([Q0, Q1, Q2, Q3, Q4]), "operationType" : NewBodyOperationType.ADD, "oppositeDirection" : true, "depth" : 5.5 * mm, "offsetDistance" : 25 * mm});
        }
        {
            var Q0;
            {var subQ0=sQuery(id+"F0.wireOp",EDGE,"E24");Q0=makeQuery(id+"F0.imprint","IMPRINT",FACE,{"disambiguationData":[TD([[makeQuery(id+"F0.imprint","IMPRINT",EDGE,{"derivedFrom":subQ0}),1.0]])]});}
            var Q1;
            {var subQ0=sQuery(id+"F0.wireOp",EDGE,"E28");Q1=makeQuery(id+"F0.imprint","IMPRINT",FACE,{"disambiguationData":[TD([[makeQuery(id+"F0.imprint","IMPRINT",EDGE,{"derivedFrom":subQ0}),1.0]])]});}
            var Q2;
            {var subQ0=sQuery(id+"F0.wireOp",EDGE,"E36");Q2=makeQuery(id+"F0.imprint","IMPRINT",FACE,{"disambiguationData":[TD([[makeQuery(id+"F0.imprint","IMPRINT",EDGE,{"derivedFrom":subQ0}),-1.0]])]});}
            extrude(context, id + "F9", {"entities" : qUnion([Q0, Q1, Q2]), "operationType" : NewBodyOperationType.REMOVE, "oppositeDirection" : true, "depth" : 3.5 * mm, "offsetDistance" : 25 * mm});
        }
        {
            var Q0;
            {var subQ0=sQuery(id+"F0.wireOp",EDGE,"E22");Q0=makeQuery(id+"F8.opExtrude","CAP_EDGE",EDGE,{"disambiguationData":[OSD([subQ0]),TDD([makeQuery(id+"F0.imprint","IMPRINT",EDGE,{"disambiguationData":[TD([[makeQuery(id+"F0.imprint","INTERSECT",VERTEX,{"derivedFrom":[subQ0,sQuery(id+"F0.wireOp",EDGE,"E24")]}),-1.0]])],"derivedFrom":subQ0})])],"isStart":false});}
            var Q1;
            {var subQ0=sQuery(id+"F0.wireOp",EDGE,"E22");Q1=makeQuery(id+"F8.opExtrude","CAP_EDGE",EDGE,{"disambiguationData":[OSD([subQ0]),TDD([makeQuery(id+"F0.imprint","IMPRINT",EDGE,{"disambiguationData":[TD([[makeQuery(id+"F0.imprint","INTERSECT",VERTEX,{"derivedFrom":[subQ0,sQuery(id+"F0.wireOp",EDGE,"E28")]}),-1.0]])],"derivedFrom":subQ0})])],"isStart":false});}
            var Q2;
            {var subQ0=sQuery(id+"F0.wireOp",EDGE,"E22");Q2=makeQuery(id+"F8.opExtrude","CAP_EDGE",EDGE,{"disambiguationData":[OSD([subQ0]),TDD([makeQuery(id+"F0.imprint","IMPRINT",EDGE,{"disambiguationData":[TD([[makeQuery(id+"F0.imprint","INTERSECT",VERTEX,{"derivedFrom":[subQ0,sQuery(id+"F0.wireOp",EDGE,"E36")]}),1.0]])],"derivedFrom":subQ0})])],"isStart":false});}
            chamfer(context, id + "F10", {"entities" : qUnion([Q0, Q1, Q2]), "chamferType" : ChamferType.OFFSET_ANGLE, "width" : 2 * mm, "oppositeDirection" : false, "angle" : 37.5 * degree, "tangentPropagation" : true});
        }
    });
